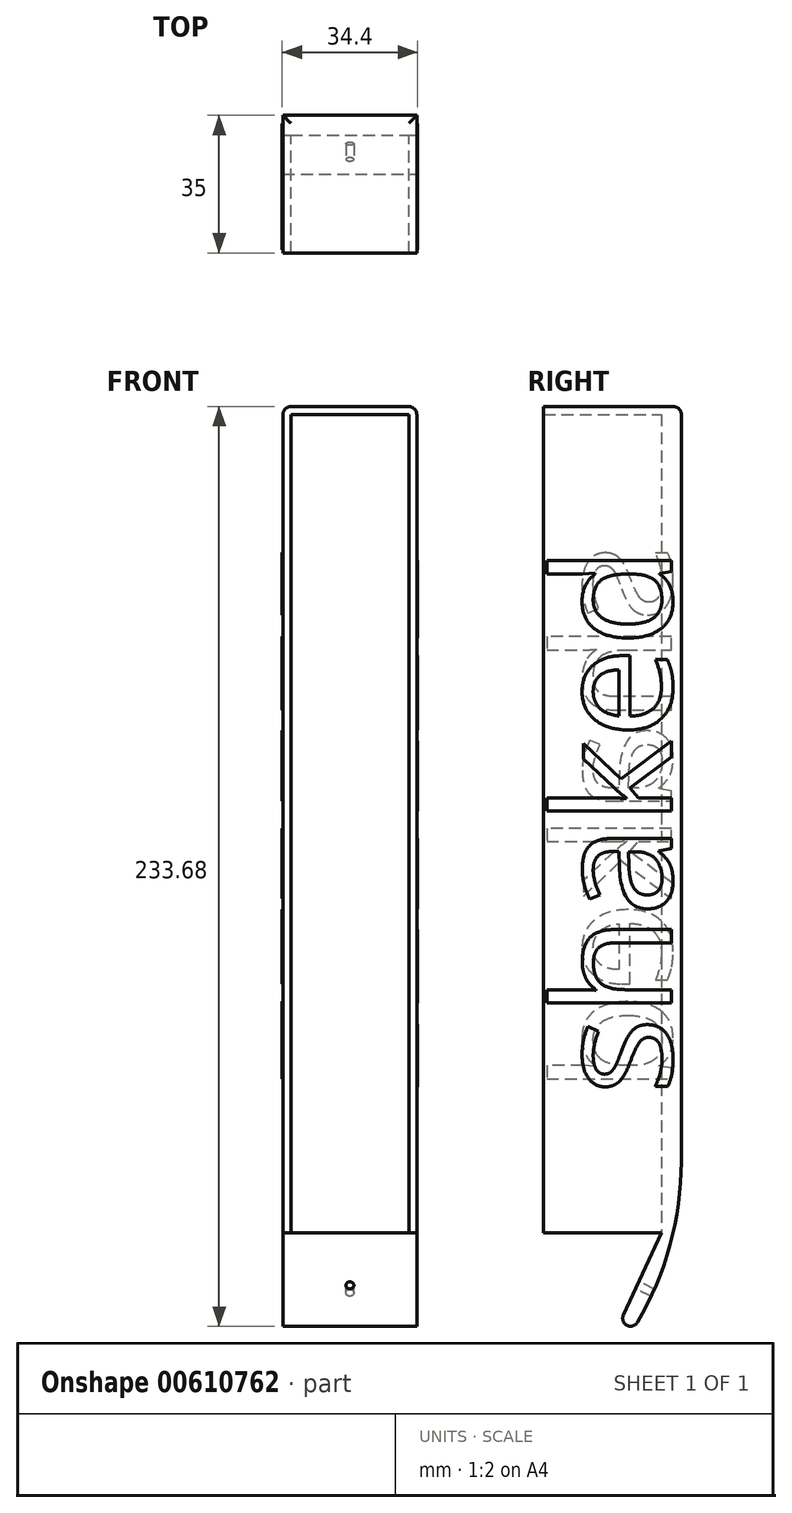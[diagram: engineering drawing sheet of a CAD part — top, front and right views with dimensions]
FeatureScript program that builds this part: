
annotation { "Feature Type Name" : "Feature", "Feature Type Description" : "" }
export const myFeature = defineFeature(function(context is Context, id is Id, definition is map)
    precondition{}
    {
        {
            var Q0;
            Q0=qCreatedBy(makeId("Front.planeOp"),FACE);
            var sketch = newSketch(context, id + "F0", { "sketchPlane" : qUnion([Q0])});
            skLineSegment(sketch, "E0.bottom", {"start": v(-13.27, 224.24) * mm, "end": v(20.73, 224.24) * mm});
            skLineSegment(sketch, "E0.top", {"start": v(-13.27, -25.76) * mm, "end": v(20.73, -25.76) * mm});
            skLineSegment(sketch, "E0.left", {"start": v(-13.27, 224.24) * mm, "end": v(-13.27, -25.76) * mm});
            skLineSegment(sketch, "E0.right", {"start": v(20.73, 224.24) * mm, "end": v(20.73, -25.76) * mm});
            skSolve(sketch);
        }
        {
            var Q0;
            Q0 = qSketchRegion(id + "F0", true);
            extrude(context, id + "F1", {"entities" : qUnion([Q0]), "depth" : 5 * mm, "offsetDistance" : 25 * mm});
        }
        {
            var Q0;
            Q0=makeQuery(id+"F1.opExtrude","CAP_FACE",FACE,{"disambiguationData":[OSD([sQuery(id+"F0.wireOp",EDGE,"E0.bottom"),sQuery(id+"F0.wireOp",EDGE,"E0.top"),sQuery(id+"F0.wireOp",EDGE,"E0.left"),sQuery(id+"F0.wireOp",EDGE,"E0.right")])],"isStart":false});
            var sketch = newSketch(context, id + "F2", { "sketchPlane" : qUnion([Q0])});
            skLineSegment(sketch, "E1.bottom", {"start": v(-13.27, 14.24) * mm, "end": v(20.73, 14.24) * mm});
            skLineSegment(sketch, "E1.top", {"start": v(-13.27, -25.76) * mm, "end": v(20.73, -25.76) * mm});
            skLineSegment(sketch, "E1.left", {"start": v(-13.27, 14.24) * mm, "end": v(-13.27, -25.76) * mm});
            skLineSegment(sketch, "E1.right", {"start": v(20.73, 14.24) * mm, "end": v(20.73, -25.76) * mm});
            skSolve(sketch);
        }
        {
            var Q0;
            Q0=makeQuery(id+"F2.imprint","IMPRINT",FACE,{"disambiguationData":[TD([[makeQuery(id+"F2.imprint","IMPRINT",EDGE,{"derivedFrom":sQuery(id+"F2.wireOp",EDGE,"E1.bottom")}),-1.0]])]});
            extrude(context, id + "F3", {"entities" : qUnion([Q0]), "operationType" : NewBodyOperationType.ADD, "depth" : 20 * mm, "offsetDistance" : 25 * mm});
        }
        {
            var Q0;
            Q0=makeQuery(id+"F1.opExtrude","CAP_EDGE",EDGE,{"disambiguationData":[OSD([sQuery(id+"F0.wireOp",EDGE,"E0.top")])],"isStart":true});
            fillet(context, id + "F4", {"entities" : qUnion([Q0]), "radius" : 80 * mm, "tangentPropagation" : true, "allowEdgeOverflow" : false});
        }
        {
            var Q0;
            Q0=makeQuery(id+"F3.opExtrude","CAP_EDGE",EDGE,{"disambiguationData":[OSD([sQuery(id+"F2.wireOp",EDGE,"E1.bottom")])],"isStart":false});
            chamfer(context, id + "F5", {"entities" : qUnion([Q0]), "chamferType" : ChamferType.OFFSET_ANGLE, "width" : 20 * mm, "oppositeDirection" : false, "angle" : 65 * degree, "tangentPropagation" : true});
        }
        {
            var Q0;
            Q0=makeQuery(id+"F1.opExtrude","CAP_FACE",FACE,{"disambiguationData":[OSD([sQuery(id+"F0.wireOp",EDGE,"E0.bottom"),sQuery(id+"F0.wireOp",EDGE,"E0.top"),sQuery(id+"F0.wireOp",EDGE,"E0.left"),sQuery(id+"F0.wireOp",EDGE,"E0.right")])],"isStart":false});
            var sketch = newSketch(context, id + "F6", { "sketchPlane" : qUnion([Q0])});
            skLineSegment(sketch, "E2.bottom", {"start": v(20.73, 224.24) * mm, "end": v(18.73, 224.24) * mm});
            skLineSegment(sketch, "E2.top", {"start": v(20.73, 14.24) * mm, "end": v(18.73, 14.24) * mm});
            skLineSegment(sketch, "E2.left", {"start": v(20.73, 224.24) * mm, "end": v(20.73, 14.24) * mm});
            skLineSegment(sketch, "E2.right", {"start": v(18.73, 224.24) * mm, "end": v(18.73, 14.24) * mm});
            skSolve(sketch);
        }
        {
            var Q0;
            {var subQ0=sQuery(id+"F6.wireOp",EDGE,"E2.right");Q0=makeQuery(id+"F6.imprint","IMPRINT",FACE,{"disambiguationData":[TD([[makeQuery(id+"F6.imprint","IMPRINT",EDGE,{"derivedFrom":subQ0}),-1.0]])]});}
            var sketch = newSketch(context, id + "F7", { "sketchPlane" : qUnion([Q0])});
            skLineSegment(sketch, "E3.bottom", {"start": v(-13.27, 224.24) * mm, "end": v(-11.27, 224.24) * mm});
            skLineSegment(sketch, "E3.top", {"start": v(-13.27, 14.24) * mm, "end": v(-11.27, 14.24) * mm});
            skLineSegment(sketch, "E3.left", {"start": v(-13.27, 224.24) * mm, "end": v(-13.27, 14.24) * mm});
            skLineSegment(sketch, "E3.right", {"start": v(-11.27, 224.24) * mm, "end": v(-11.27, 14.24) * mm});
            skSolve(sketch);
        }
        {
            var Q0;
            Q0=makeQuery(id+"F6.imprint","IMPRINT",FACE,{"disambiguationData":[TD([[makeQuery(id+"F6.imprint","IMPRINT",EDGE,{"derivedFrom":sQuery(id+"F6.wireOp",EDGE,"E2.bottom")}),-1.0]])]});
            extrude(context, id + "F8", {"entities" : qUnion([Q0]), "operationType" : NewBodyOperationType.ADD, "depth" : 30 * mm, "offsetDistance" : 25 * mm});
        }
        {
            var Q0;
            Q0=makeQuery(id+"F7.imprint","IMPRINT",FACE,{"disambiguationData":[TD([[makeQuery(id+"F7.imprint","IMPRINT",EDGE,{"derivedFrom":sQuery(id+"F7.wireOp",EDGE,"E3.bottom")}),-1.0]])]});
            extrude(context, id + "F9", {"entities" : qUnion([Q0]), "operationType" : NewBodyOperationType.ADD, "depth" : 30 * mm, "offsetDistance" : 25 * mm});
        }
        {
            var Q0;
            Q0=makeQuery(id+"F1.opExtrude","CAP_FACE",FACE,{"disambiguationData":[OSD([sQuery(id+"F0.wireOp",EDGE,"E0.bottom"),sQuery(id+"F0.wireOp",EDGE,"E0.top"),sQuery(id+"F0.wireOp",EDGE,"E0.left"),sQuery(id+"F0.wireOp",EDGE,"E0.right")])],"isStart":false});
            var sketch = newSketch(context, id + "F10", { "sketchPlane" : qUnion([Q0])});
            skLineSegment(sketch, "E4.bottom", {"start": v(-11.27, 224.24) * mm, "end": v(18.73, 224.24) * mm});
            skLineSegment(sketch, "E4.top", {"start": v(-11.27, 222.24) * mm, "end": v(18.73, 222.24) * mm});
            skLineSegment(sketch, "E4.left", {"start": v(-11.27, 224.24) * mm, "end": v(-11.27, 222.24) * mm});
            skLineSegment(sketch, "E4.right", {"start": v(18.73, 224.24) * mm, "end": v(18.73, 222.24) * mm});
            skSolve(sketch);
        }
        {
            var Q0;
            Q0 = qSketchRegion(id + "F10", true);
            extrude(context, id + "F11", {"entities" : qUnion([Q0]), "operationType" : NewBodyOperationType.ADD, "depth" : 30 * mm, "offsetDistance" : 25 * mm});
        }
        {
            var Q0;
            Q0=makeQuery(id+"F8.boolean.opBoolean","MERGE",FACE,{"derivedFrom":[makeQuery(id+"F3.boolean.opBoolean","MERGE",FACE,{"derivedFrom":[makeQuery(id+"F1.opExtrude","SWEPT_FACE",FACE,{"disambiguationData":[OSD([sQuery(id+"F0.wireOp",EDGE,"E0.right")])]}),makeQuery(id+"F3.opExtrude","SWEPT_FACE",FACE,{"disambiguationData":[OSD([sQuery(id+"F2.wireOp",EDGE,"E1.right")])]})]}),makeQuery(id+"F8.opExtrude","SWEPT_FACE",FACE,{"disambiguationData":[OSD([sQuery(id+"F6.wireOp",EDGE,"E2.left")])]})]});
            var sketch = newSketch(context, id + "F12", { "sketchPlane" : qUnion([Q0])});
            skText(sketch, "E5", { "text": "shaked", "fontName": "OpenSans-Regular.ttf"});
            const initialGuessF12  = {"E5": [-0.0025, 0.04924, 0, 1, 0.03]};
            skSetInitialGuess(sketch, initialGuessF12);
            skSolve(sketch);
        }
        {
            var Q0;
            Q0 = qSketchRegion(id + "F12", true);
            extrude(context, id + "F13", {"entities" : qUnion([Q0]), "operationType" : NewBodyOperationType.ADD, "depth" : 0.2 * mm, "offsetDistance" : 25 * mm});
        }
        {
            var Q0;
            Q0=makeQuery(id+"F9.boolean.opBoolean","MERGE",FACE,{"derivedFrom":[makeQuery(id+"F3.boolean.opBoolean","MERGE",FACE,{"derivedFrom":[makeQuery(id+"F1.opExtrude","SWEPT_FACE",FACE,{"disambiguationData":[OSD([sQuery(id+"F0.wireOp",EDGE,"E0.left")])]}),makeQuery(id+"F3.opExtrude","SWEPT_FACE",FACE,{"disambiguationData":[OSD([sQuery(id+"F2.wireOp",EDGE,"E1.left")])]})]}),makeQuery(id+"F9.opExtrude","SWEPT_FACE",FACE,{"disambiguationData":[OSD([sQuery(id+"F7.wireOp",EDGE,"E3.left")])]})]});
            var sketch = newSketch(context, id + "F14", { "sketchPlane" : qUnion([Q0])});
            skText(sketch, "E6", { "text": "shaked", "fontName": "OpenSans-Regular.ttf"});
            const initialGuessF14  = {"E6": [0.0025, 0.18924, 0, -1, 0.03]};
            skSetInitialGuess(sketch, initialGuessF14);
            skSolve(sketch);
        }
        {
            var Q0;
            Q0 = qSketchRegion(id + "F14", true);
            extrude(context, id + "F15", {"entities" : qUnion([Q0]), "operationType" : NewBodyOperationType.ADD, "depth" : 0.2 * mm, "offsetDistance" : 25 * mm});
        }
        {
            var Q0;
            Q0=makeQuery(id+"F9.boolean.opBoolean","MERGE",EDGE,{"derivedFrom":[makeQuery(id+"F1.opExtrude","SWEPT_EDGE",EDGE,{"disambiguationData":[OSD([sQuery(id+"F0.wireOp",EDGE,"E0.bottom"),sQuery(id+"F0.wireOp",EDGE,"E0.left")])]}),makeQuery(id+"F9.opExtrude","SWEPT_EDGE",EDGE,{"disambiguationData":[OSD([sQuery(id+"F7.wireOp",EDGE,"E3.bottom"),sQuery(id+"F7.wireOp",EDGE,"E3.left")])]})]});
            var Q1;
            Q1=makeQuery(id+"F8.boolean.opBoolean","MERGE",EDGE,{"derivedFrom":[makeQuery(id+"F1.opExtrude","SWEPT_EDGE",EDGE,{"disambiguationData":[OSD([sQuery(id+"F0.wireOp",EDGE,"E0.bottom"),sQuery(id+"F0.wireOp",EDGE,"E0.right")])]}),makeQuery(id+"F8.opExtrude","SWEPT_EDGE",EDGE,{"disambiguationData":[OSD([sQuery(id+"F6.wireOp",EDGE,"E2.bottom"),sQuery(id+"F6.wireOp",EDGE,"E2.left")])]})]});
            var Q2;
            Q2=makeQuery(id+"F1.opExtrude","CAP_EDGE",EDGE,{"disambiguationData":[OSD([sQuery(id+"F0.wireOp",EDGE,"E0.bottom")])],"isStart":true});
            var Q3;
            Q3=makeQuery(id+"F5.opChamfer","BLEND_EDGE",EDGE,{"blendedFrom":[makeQuery(id+"F3.opExtrude","CAP_EDGE",EDGE,{"disambiguationData":[OSD([sQuery(id+"F2.wireOp",EDGE,"E1.bottom")])],"isStart":false}),makeQuery(id+"F4.opFillet","BLEND_FACE",FACE,{"disambiguationData":[OSD([sQuery(id+"F0.wireOp",EDGE,"E0.top")])]})],"blendedInto":[makeQuery(id+"F4.opFillet","BLEND_FACE",FACE,{"disambiguationData":[OSD([sQuery(id+"F0.wireOp",EDGE,"E0.top")])]})]});
            fillet(context, id + "F16", {"entities" : qUnion([Q0, Q1, Q2, Q3]), "radius" : 2 * mm, "tangentPropagation" : true, "allowEdgeOverflow" : false});
        }
        {
            var Q0;
            Q0=makeQuery(id+"F5.opChamfer","BLEND_FACE",FACE,{"disambiguationData":[OSD([sQuery(id+"F2.wireOp",EDGE,"E1.bottom")])]});
            var sketch = newSketch(context, id + "F17", { "sketchPlane" : qUnion([Q0])});
            skCircle(sketch, "E7", {"center": v(3.73, -3.88) * mm, "radius": 1 * mm});
            skSolve(sketch);
        }
        {
            var Q0;
            Q0=makeQuery(id+"F17.imprint","IMPRINT",FACE,{"disambiguationData":[TD([[makeQuery(id+"F17.imprint","IMPRINT",EDGE,{"derivedFrom":sQuery(id+"F17.wireOp",EDGE,"E7")}),1.0]])]});
            extrude(context, id + "F18", {"entities" : qUnion([Q0]), "operationType" : NewBodyOperationType.REMOVE, "oppositeDirection" : true, "depth" : 10 * mm, "offsetDistance" : 25 * mm});
        }
    });
